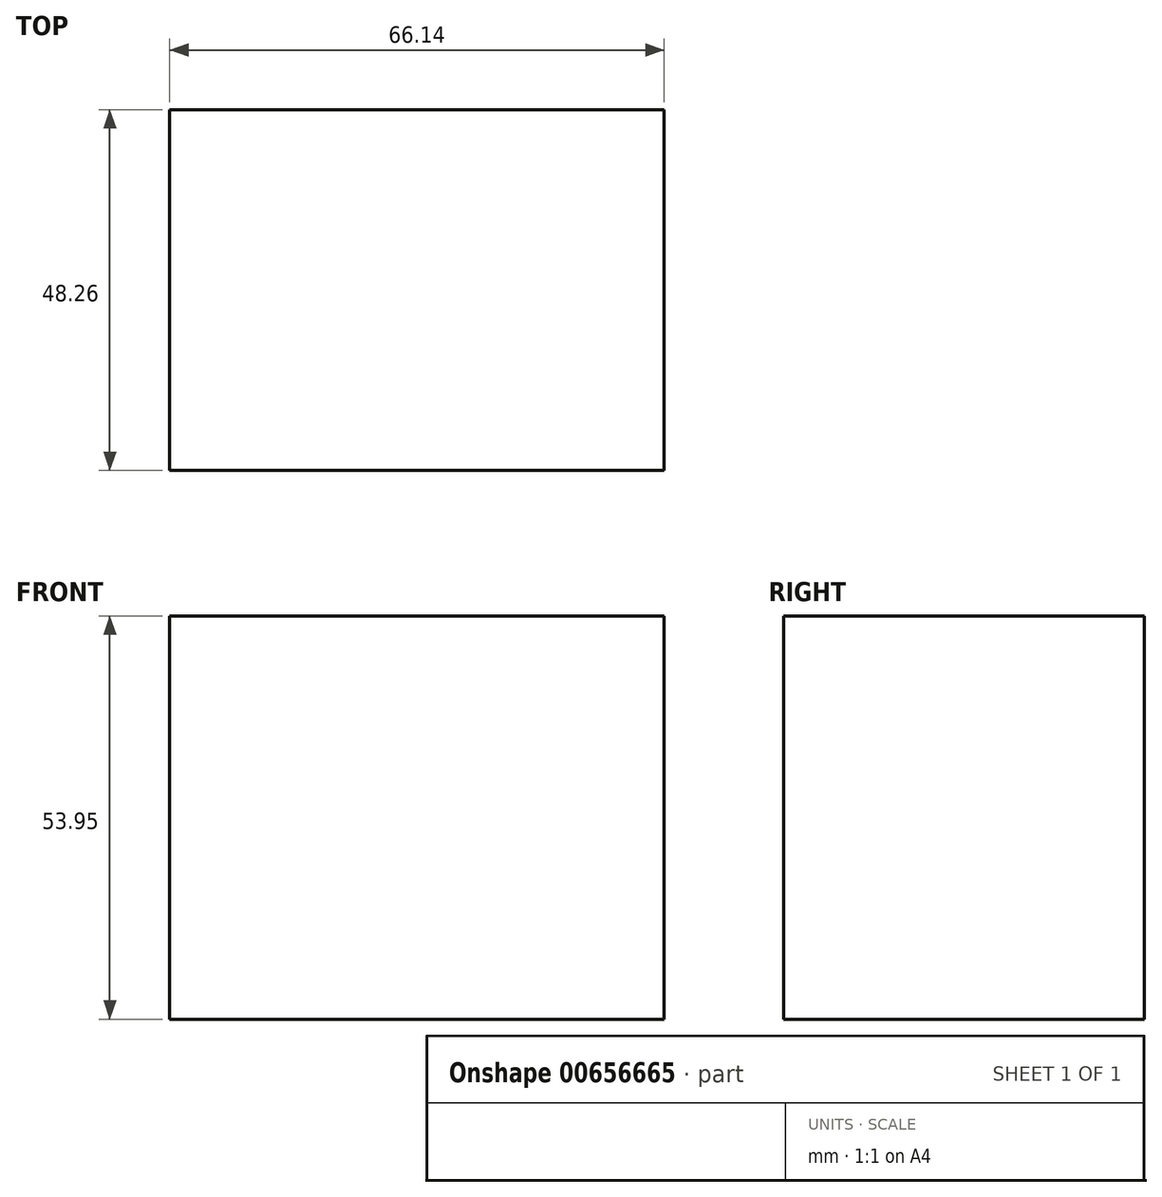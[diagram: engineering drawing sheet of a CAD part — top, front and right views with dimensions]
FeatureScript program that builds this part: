
annotation { "Feature Type Name" : "Feature", "Feature Type Description" : "" }
export const myFeature = defineFeature(function(context is Context, id is Id, definition is map)
    precondition{}
    {
        {
            var Q0;
            Q0=qCreatedBy(makeId("Front.planeOp"),FACE);
            var sketch = newSketch(context, id + "F0", { "sketchPlane" : qUnion([Q0])});
            skLineSegment(sketch, "E0.bottom", {"start": v(-38.25, 10.67) * mm, "end": v(27.89, 10.67) * mm});
            skLineSegment(sketch, "E0.top", {"start": v(-38.25, 64.62) * mm, "end": v(27.89, 64.62) * mm});
            skLineSegment(sketch, "E0.left", {"start": v(-38.25, 10.67) * mm, "end": v(-38.25, 64.62) * mm});
            skLineSegment(sketch, "E0.right", {"start": v(27.89, 10.67) * mm, "end": v(27.89, 64.62) * mm});
            skLineSegment(sketch, "E1", {"start": v(-16.3, 45.11) * mm, "end": v(3.81, 45.11) * mm});
            skLineSegment(sketch, "E2", {"start": v(-6.25, 45.11) * mm, "end": v(-6.25, 28.96) * mm});
            skSolve(sketch);
        }
        {
            var Q0;
            Q0 = qSketchRegion(id + "F0", true);
            extrude(context, id + "F1", {"entities" : qUnion([Q0]), "depth" : 48.26 * mm, "offsetDistance" : 25.4 * mm});
        }
    });
